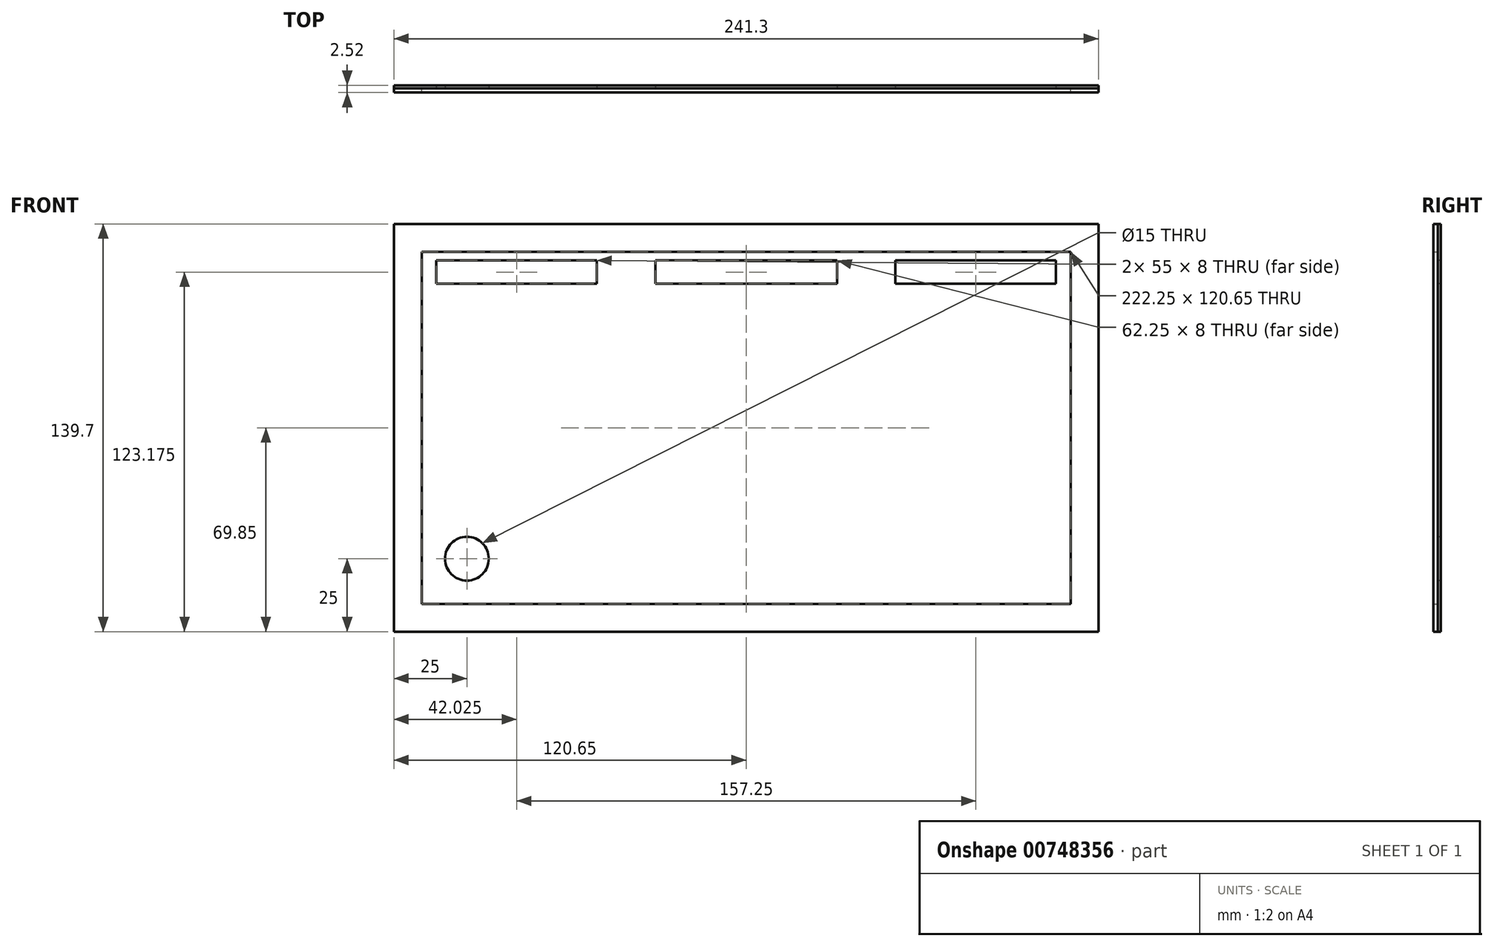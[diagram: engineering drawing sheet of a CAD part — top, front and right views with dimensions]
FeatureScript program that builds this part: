
annotation { "Feature Type Name" : "Feature", "Feature Type Description" : "" }
export const myFeature = defineFeature(function(context is Context, id is Id, definition is map)
    precondition{}
    {
        {
            var Q0;
            Q0=qCreatedBy(makeId("Front.planeOp"),FACE);
            var sketch = newSketch(context, id + "F0", { "sketchPlane" : qUnion([Q0])});
            skLineSegment(sketch, "E0.bottom", {"start": v(120.65, -69.85) * mm, "end": v(-120.65, -69.85) * mm});
            skLineSegment(sketch, "E0.top", {"start": v(120.65, 69.85) * mm, "end": v(-120.65, 69.85) * mm});
            skLineSegment(sketch, "E0.left", {"start": v(120.65, -69.85) * mm, "end": v(120.65, 69.85) * mm});
            skLineSegment(sketch, "E0.right", {"start": v(-120.65, -69.85) * mm, "end": v(-120.65, 69.85) * mm});
            skPoint(sketch, "E0.middle", {"position": v(0, 0) * mm});
            skSolve(sketch);
        }
        {
            var Q0;
            Q0=makeQuery(id+"F0.imprint","IMPRINT",FACE,{"disambiguationData":[TD([[makeQuery(id+"F0.imprint","IMPRINT",EDGE,{"derivedFrom":sQuery(id+"F0.wireOp",EDGE,"E0.bottom")}),-1.0]])]});
            extrude(context, id + "F1", {"entities" : qUnion([Q0]), "depth" : 1.02 * mm, "offsetDistance" : 25 * mm});
        }
        {
            var Q0;
            Q0=makeQuery(id+"F1.opExtrude","CAP_FACE",FACE,{"disambiguationData":[OSD([sQuery(id+"F0.wireOp",EDGE,"E0.bottom"),sQuery(id+"F0.wireOp",EDGE,"E0.top"),sQuery(id+"F0.wireOp",EDGE,"E0.left"),sQuery(id+"F0.wireOp",EDGE,"E0.right")])],"isStart":false});
            var sketch = newSketch(context, id + "F2", { "sketchPlane" : qUnion([Q0])});
            skLineSegment(sketch, "E1.0", {"start": v(120.65, 69.85) * mm, "end": v(-120.65, 69.85) * mm});
            skLineSegment(sketch, "E2.0", {"start": v(-120.65, -69.85) * mm, "end": v(-120.65, 69.85) * mm});
            skLineSegment(sketch, "E3.0", {"start": v(120.65, -69.85) * mm, "end": v(-120.65, -69.85) * mm});
            skLineSegment(sketch, "E4.0", {"start": v(120.65, -69.85) * mm, "end": v(120.65, 69.85) * mm});
            skLineSegment(sketch, "E5.0", {"start": v(111.12, 60.33) * mm, "end": v(-111.12, 60.32) * mm});
            skLineSegment(sketch, "E5.1", {"start": v(111.12, -60.32) * mm, "end": v(111.12, 60.33) * mm});
            skLineSegment(sketch, "E5.2", {"start": v(111.12, -60.32) * mm, "end": v(-111.12, -60.33) * mm});
            skLineSegment(sketch, "E5.3", {"start": v(-111.12, -60.33) * mm, "end": v(-111.12, 60.32) * mm});
            skLineSegment(sketch, "E6.0", {"start": v(121.65, 70.85) * mm, "end": v(-121.65, 70.85) * mm});
            skLineSegment(sketch, "E6.1", {"start": v(121.65, -70.85) * mm, "end": v(121.65, 70.85) * mm});
            skLineSegment(sketch, "E6.2", {"start": v(121.65, -70.85) * mm, "end": v(-121.65, -70.85) * mm});
            skLineSegment(sketch, "E6.3", {"start": v(-121.65, -70.85) * mm, "end": v(-121.65, 70.85) * mm});
            skSolve(sketch);
        }
        {
            var Q0;
            Q0=makeQuery(id+"F2.imprint","IMPRINT",FACE,{"disambiguationData":[TD([[makeQuery(id+"F2.imprint","IMPRINT",EDGE,{"derivedFrom":sQuery(id+"F2.wireOp",EDGE,"E5.0")}),1.0]])]});
            var sketch = newSketch(context, id + "F3", { "sketchPlane" : qUnion([Q0])});
            skCircle(sketch, "E7", {"center": v(-95.65, -44.85) * mm, "radius": 7.5 * mm});
            skLineSegment(sketch, "E8.bottom", {"start": v(-106.12, 57.32) * mm, "end": v(-51.12, 57.33) * mm});
            skLineSegment(sketch, "E8.top", {"start": v(-106.12, 49.32) * mm, "end": v(-51.12, 49.33) * mm});
            skLineSegment(sketch, "E8.left", {"start": v(-106.12, 57.32) * mm, "end": v(-106.12, 49.32) * mm});
            skLineSegment(sketch, "E8.right", {"start": v(-51.12, 57.33) * mm, "end": v(-51.12, 49.33) * mm});
            skLineSegment(sketch, "E9.0", {"start": v(111.12, 60.33) * mm, "end": v(-111.12, 60.32) * mm});
            skLineSegment(sketch, "E10.bottom", {"start": v(51.12, 57.33) * mm, "end": v(106.12, 57.33) * mm});
            skLineSegment(sketch, "E10.top", {"start": v(51.12, 49.33) * mm, "end": v(106.12, 49.33) * mm});
            skLineSegment(sketch, "E10.left", {"start": v(51.13, 57.33) * mm, "end": v(51.13, 49.33) * mm});
            skLineSegment(sketch, "E10.right", {"start": v(106.12, 57.33) * mm, "end": v(106.12, 49.33) * mm});
            skLineSegment(sketch, "E11.bottom", {"start": v(-31.12, 57.33) * mm, "end": v(31.12, 57.33) * mm});
            skLineSegment(sketch, "E11.top", {"start": v(-31.12, 49.32) * mm, "end": v(31.12, 49.33) * mm});
            skLineSegment(sketch, "E11.left", {"start": v(-31.12, 57.33) * mm, "end": v(-31.12, 49.33) * mm});
            skLineSegment(sketch, "E11.right", {"start": v(31.12, 57.33) * mm, "end": v(31.12, 49.33) * mm});
            skLineSegment(sketch, "E12.0", {"start": v(-111.12, -60.33) * mm, "end": v(-111.12, 60.32) * mm});
            skLineSegment(sketch, "E13.0", {"start": v(111.12, -60.32) * mm, "end": v(-111.12, -60.33) * mm});
            skLineSegment(sketch, "E14.0", {"start": v(111.12, -60.32) * mm, "end": v(111.12, 60.33) * mm});
            skLineSegment(sketch, "E15.0", {"start": v(-120.65, -69.85) * mm, "end": v(-120.65, 69.85) * mm});
            skLineSegment(sketch, "E16.0", {"start": v(120.65, -69.85) * mm, "end": v(-120.65, -69.85) * mm});
            skLineSegment(sketch, "E17.0", {"start": v(120.65, -69.85) * mm, "end": v(120.65, 69.85) * mm});
            skLineSegment(sketch, "E18.0", {"start": v(120.65, 69.85) * mm, "end": v(-120.65, 69.85) * mm});
            skSolve(sketch);
        }
        {
            var Q0;
            Q0=makeQuery(id+"F3.imprint","IMPRINT",FACE,{"disambiguationData":[TD([[makeQuery(id+"F3.imprint","IMPRINT",EDGE,{"derivedFrom":sQuery(id+"F3.wireOp",EDGE,"E7")}),1.0]])]});
            var Q1;
            Q1=makeQuery(id+"F3.imprint","IMPRINT",FACE,{"disambiguationData":[TD([[makeQuery(id+"F3.imprint","IMPRINT",EDGE,{"derivedFrom":sQuery(id+"F3.wireOp",EDGE,"E8.bottom")}),-1.0]])]});
            var Q2;
            Q2=makeQuery(id+"F3.imprint","IMPRINT",FACE,{"disambiguationData":[TD([[makeQuery(id+"F3.imprint","IMPRINT",EDGE,{"derivedFrom":sQuery(id+"F3.wireOp",EDGE,"E11.bottom")}),-1.0]])]});
            var Q3;
            Q3=makeQuery(id+"F3.imprint","IMPRINT",FACE,{"disambiguationData":[TD([[makeQuery(id+"F3.imprint","IMPRINT",EDGE,{"derivedFrom":sQuery(id+"F3.wireOp",EDGE,"E10.bottom")}),-1.0]])]});
            extrude(context, id + "F4", {"entities" : qUnion([Q0, Q1, Q2, Q3]), "operationType" : NewBodyOperationType.REMOVE, "endBound" : BoundingType.THROUGH_ALL, "oppositeDirection" : true, "depth" : 25 * mm, "offsetDistance" : 25 * mm});
        }
        {
            var Q0;
            Q0=makeQuery(id+"F2.imprint","IMPRINT",FACE,{"disambiguationData":[TD([[makeQuery(id+"F2.imprint","IMPRINT",EDGE,{"derivedFrom":sQuery(id+"F2.wireOp",EDGE,"E1.0")}),1.0]])]});
            extrude(context, id + "F5", {"entities" : qUnion([Q0]), "depth" : 1.5 * mm, "offsetDistance" : 25 * mm});
        }
    });
